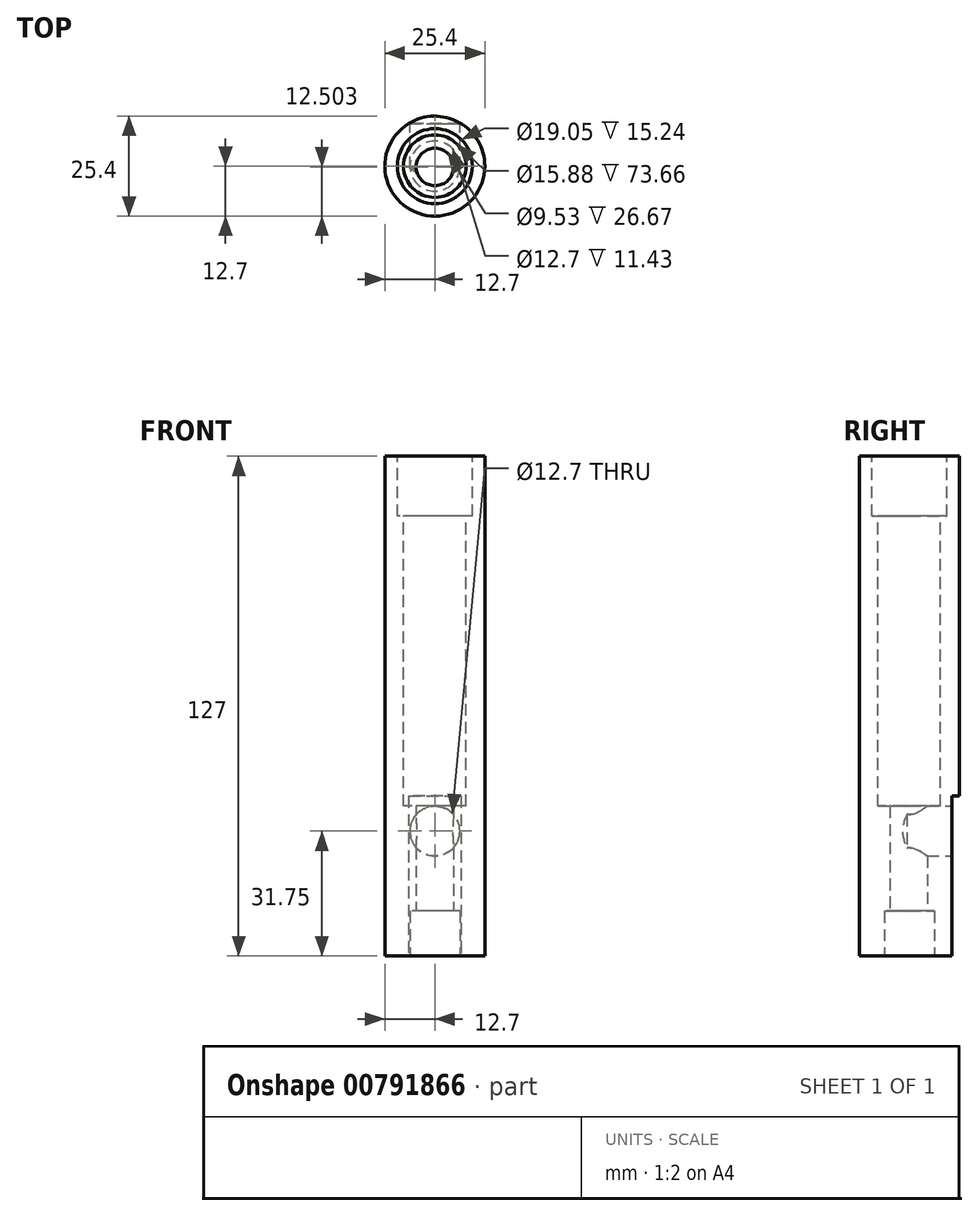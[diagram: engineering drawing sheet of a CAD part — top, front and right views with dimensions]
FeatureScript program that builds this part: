
annotation { "Feature Type Name" : "Feature", "Feature Type Description" : "" }
export const myFeature = defineFeature(function(context is Context, id is Id, definition is map)
    precondition{}
    {
        {
            var Q0;
            Q0=qCreatedBy(makeId("Top.planeOp"),FACE);
            var sketch = newSketch(context, id + "F0", { "sketchPlane" : qUnion([Q0])});
            skCircle(sketch, "E0", {"center": v(0, 0) * mm, "radius": 12.7 * mm});
            skSolve(sketch);
        }
        {
            var Q0;
            Q0=makeQuery(id+"F0.imprint","IMPRINT",FACE,{"disambiguationData":[TD([[makeQuery(id+"F0.imprint","IMPRINT",EDGE,{"derivedFrom":sQuery(id+"F0.wireOp",EDGE,"E0")}),1.0]])]});
            extrude(context, id + "F1", {"entities" : qUnion([Q0]), "depth" : 127 * mm, "offsetDistance" : 25.4 * mm});
        }
        {
            var Q0;
            Q0=makeQuery(id+"F1.opExtrude","CAP_FACE",FACE,{"disambiguationData":[OSD([sQuery(id+"F0.wireOp",EDGE,"E0")])],"isStart":false});
            var sketch = newSketch(context, id + "F2", { "sketchPlane" : qUnion([Q0])});
            skCircle(sketch, "E1", {"center": v(0, 0) * mm, "radius": 7.94 * mm});
            skSolve(sketch);
        }
        {
            var Q0;
            Q0=makeQuery(id+"F2.imprint","IMPRINT",FACE,{"disambiguationData":[TD([[makeQuery(id+"F2.imprint","IMPRINT",EDGE,{"derivedFrom":sQuery(id+"F2.wireOp",EDGE,"E1")}),1.0]])]});
            extrude(context, id + "F3", {"entities" : qUnion([Q0]), "operationType" : NewBodyOperationType.REMOVE, "oppositeDirection" : true, "depth" : 88.9 * mm, "offsetDistance" : 25.4 * mm});
        }
        {
            var Q0;
            Q0=makeQuery(id+"F1.opExtrude","CAP_FACE",FACE,{"disambiguationData":[OSD([sQuery(id+"F0.wireOp",EDGE,"E0")])],"isStart":true});
            var sketch = newSketch(context, id + "F4", { "sketchPlane" : qUnion([Q0])});
            skCircle(sketch, "E2", {"center": v(0, 0.2) * mm, "radius": 4.76 * mm});
            skSolve(sketch);
        }
        {
            var Q0;
            Q0=makeQuery(id+"F1.opExtrude","CAP_FACE",FACE,{"disambiguationData":[OSD([sQuery(id+"F0.wireOp",EDGE,"E0")])],"isStart":true});
            var sketch = newSketch(context, id + "F5", { "sketchPlane" : qUnion([Q0])});
            skLineSegment(sketch, "E3.bottom", {"start": v(-10.16, -15.88) * mm, "end": v(10.16, -15.88) * mm});
            skLineSegment(sketch, "E3.top", {"start": v(-10.16, -10.8) * mm, "end": v(10.16, -10.8) * mm});
            skLineSegment(sketch, "E3.left", {"start": v(-10.16, -15.88) * mm, "end": v(-10.16, -10.8) * mm});
            skLineSegment(sketch, "E3.right", {"start": v(10.16, -15.88) * mm, "end": v(10.16, -10.8) * mm});
            skSolve(sketch);
        }
        {
            var Q0;
            {var subQ0=sQuery(id+"F5.wireOp",EDGE,"E3.top");var subQ1=makeQuery(id+"F1.opExtrude","CAP_EDGE",EDGE,{"disambiguationData":[OSD([sQuery(id+"F0.wireOp",EDGE,"E0")])],"isStart":true});var subQ2=makeQuery(id+"F5.imprint","INTERSECT",VERTEX,{"disambiguationData":[OD(0.0)],"derivedFrom":[subQ1,subQ0]});Q0=makeQuery(id+"F5.imprint","IMPRINT",FACE,{"disambiguationData":[TD([[makeQuery(id+"F5.imprint","IMPRINT",EDGE,{"disambiguationData":[TD([[subQ2,-1.0]])],"derivedFrom":subQ0}),-1.0]])]});}
            extrude(context, id + "F6", {"entities" : qUnion([Q0]), "operationType" : NewBodyOperationType.REMOVE, "oppositeDirection" : true, "depth" : 40.64 * mm, "offsetDistance" : 25.4 * mm});
        }
        {
            var Q0;
            Q0=makeQuery(id+"F6.boolean.opBoolean","COPY",FACE,{"derivedFrom":makeQuery(id+"F6.opExtrude","SWEPT_FACE",FACE,{"disambiguationData":[OSD([sQuery(id+"F5.wireOp",EDGE,"E3.top")])]})});
            var sketch = newSketch(context, id + "F7", { "sketchPlane" : qUnion([Q0])});
            skPoint(sketch, "E4", {"position": v(0, 31.75) * mm});
            skSolve(sketch);
        }
        {
            var Q0;
            Q0=makeQuery(id+"F1.opExtrude","CAP_FACE",FACE,{"disambiguationData":[OSD([sQuery(id+"F0.wireOp",EDGE,"E0")])],"isStart":false});
            var sketch = newSketch(context, id + "F8", { "sketchPlane" : qUnion([Q0])});
            skCircle(sketch, "E5", {"center": v(0, 0) * mm, "radius": 9.53 * mm});
            skSolve(sketch);
        }
        {
            var Q0;
            Q0 = qSketchRegion(id + "F8", true);
            extrude(context, id + "F9", {"entities" : qUnion([Q0]), "operationType" : NewBodyOperationType.REMOVE, "oppositeDirection" : true, "depth" : 15.24 * mm, "offsetDistance" : 25.4 * mm});
        }
        {
            var Q0;
            Q0=sQuery(id+"F7.wireOp",VERTEX,"E4");
            var Q1;
            Q1=makeQuery(id+"F1.opExtrude","SWEPT_BODY",BODY,{"disambiguationData":[OSD([sQuery(id+"F0.wireOp",EDGE,"E0")])]});
            hole(context, id + "F10", {"style" : HoleStyle.SIMPLE, "endStyle" : HoleEndStyle.BLIND, "holeDiameter" : 12.7 * mm, "majorDiameter" : 6.35 * mm, "holeDepth" : 11.43 * mm, "isTappedThrough" : true, "tappedDepth" : 12.7 * mm, "tapClearance" : 3, "startFromSketch" : true, "locations" : qUnion([Q0]), "scope" : qUnion([Q1])});
        }
        {
            var Q0;
            Q0 = qSketchRegion(id + "F4", true);
            extrude(context, id + "F11", {"entities" : qUnion([Q0]), "operationType" : NewBodyOperationType.REMOVE, "oppositeDirection" : true, "depth" : 50.8 * mm, "offsetDistance" : 25.4 * mm});
        }
        {
            var Q0;
            Q0=qCreatedBy(makeId("Top.planeOp"),FACE);
            var sketch = newSketch(context, id + "F12", { "sketchPlane" : qUnion([Q0])});
            skCircle(sketch, "E6", {"center": v(0, 0) * mm, "radius": 6.35 * mm});
            skSolve(sketch);
        }
        {
            var Q0;
            Q0=makeQuery(id+"F12.imprint","IMPRINT",FACE,{"disambiguationData":[TD([[makeQuery(id+"F12.imprint","IMPRINT",EDGE,{"derivedFrom":sQuery(id+"F12.wireOp",EDGE,"E6")}),1.0]])]});
            extrude(context, id + "F13", {"entities" : qUnion([Q0]), "operationType" : NewBodyOperationType.REMOVE, "depth" : 11.43 * mm, "offsetDistance" : 25.4 * mm});
        }
    });
